# Revit family: P190780JX-205c_JF42NXFXDE_WoodPanel_JA_Refrigeration_Built-in
name_source: partatom
category: Specialty Equipment
units: mm (PartAtom-declared; Revit-internal decimal feet)

## family parameters
Always vertical = Yes
Cut with Voids When Loaded = No
Enable Cutting in Views = No
Maintain Annotation Orientation = No
Part Type = Normal
Room Calculation Point = No
Round Connector Dimension = Use Diameter
Shared = No
Work Plane-Based = No

## types (1)
- JF42NXFXDE
    Accent Material = ARCAT - Metal - Steel - Black
    Amps = 0 A
    Body Material = ARCAT - Metal - Steel - Stainless
    Clearance Material = ARCAT - Clearance
    Default Elevation = 0"
    Depth = 26 7/8"
    Door Material = ARCAT - Thermal - Wood Fiber Cover Board
    Family Name = 42" BIR Panel Kits - JS42NXFXDE
    Handle Material = ARCAT - Metal - Steel - Stainless
    Height = 82 7/8"
    Manufacturer = Jenn Air
    Model = JF42NXFXDE
    Voltage = 0 V
    Wheel Material = ARCAT - Plastic - Black
    Width = 41 3/4"

## geometry (parser evidence)
native form markers: Sweep x3
no freeform markers — native parametric forms only
